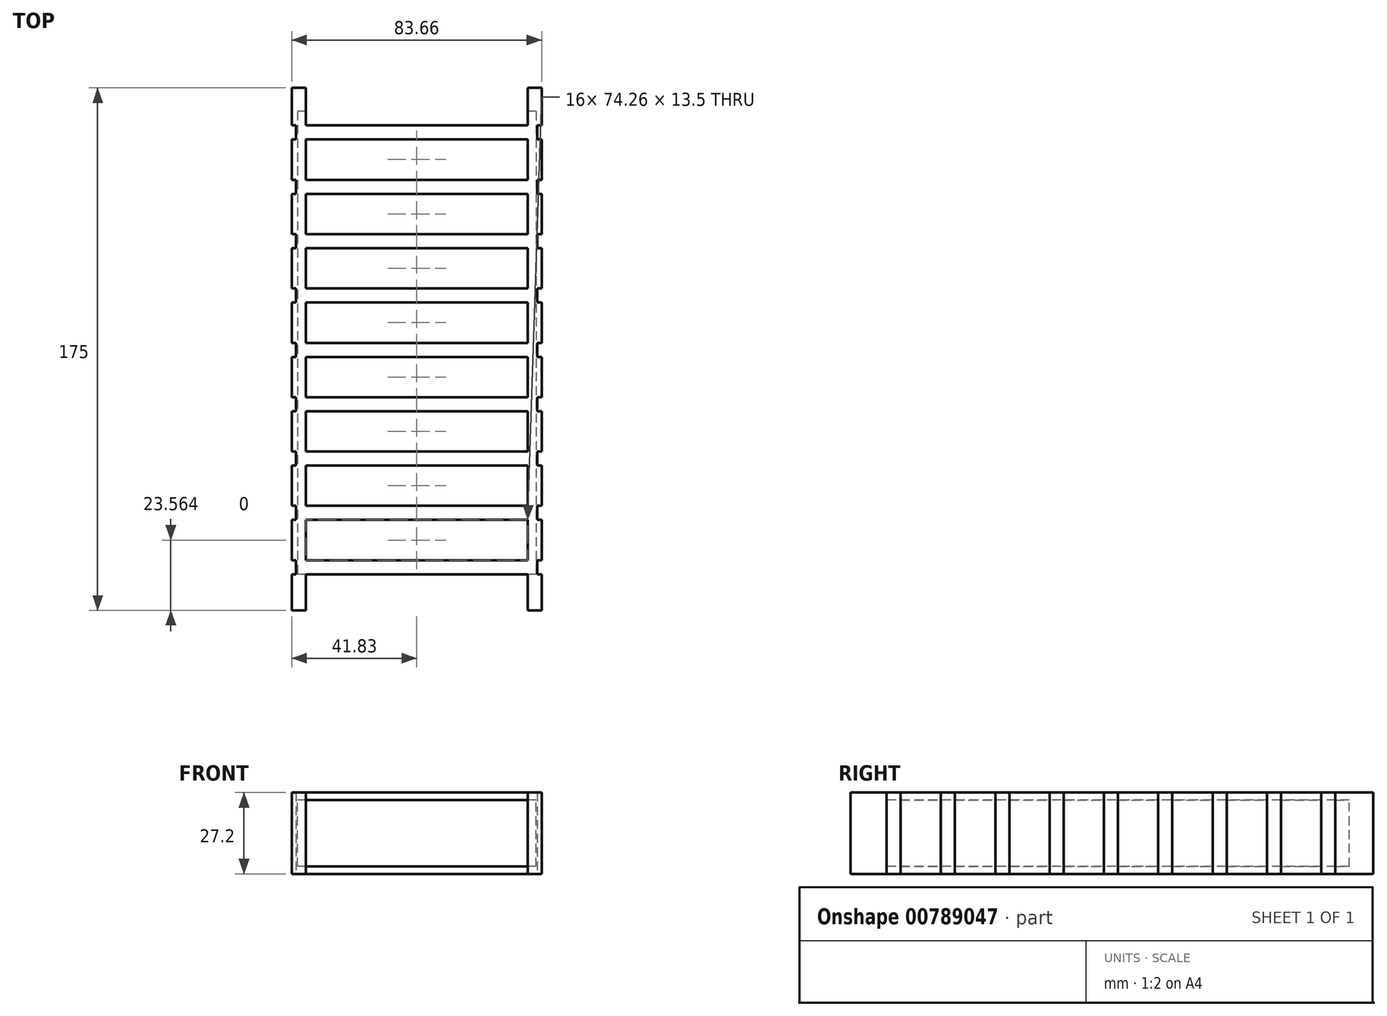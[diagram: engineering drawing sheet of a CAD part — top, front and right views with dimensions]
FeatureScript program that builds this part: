
annotation { "Feature Type Name" : "Feature", "Feature Type Description" : "" }
export const myFeature = defineFeature(function(context is Context, id is Id, definition is map)
    precondition{}
    {
        {
            var Q0;
            Q0=qCreatedBy(makeId("Top.planeOp"),FACE);
            var sketch = newSketch(context, id + "F0", { "sketchPlane" : qUnion([Q0])});
            skLineSegment(sketch, "E0.bottom", {"start": v(-37.13, -87.5) * mm, "end": v(-41.83, -87.5) * mm});
            skLineSegment(sketch, "E0.top", {"start": v(-37.13, 87.5) * mm, "end": v(-41.83, 87.5) * mm});
            skLineSegment(sketch, "E0.left", {"start": v(-37.13, -87.5) * mm, "end": v(-37.13, 87.5) * mm});
            skLineSegment(sketch, "E0.right", {"start": v(-41.83, -87.5) * mm, "end": v(-41.83, 87.5) * mm});
            skPoint(sketch, "E0.middle", {"position": v(-39.48, 0) * mm});
            skLineSegment(sketch, "E1.MirrorCS", {"start": v(37.13, -87.5) * mm, "end": v(41.83, -87.5) * mm});
            skLineSegment(sketch, "E2.MirrorCS", {"start": v(37.13, 87.5) * mm, "end": v(41.83, 87.5) * mm});
            skLineSegment(sketch, "E3.MirrorCS", {"start": v(41.83, -87.5) * mm, "end": v(41.83, 87.5) * mm});
            skLineSegment(sketch, "E4.MirrorCS", {"start": v(37.13, -87.5) * mm, "end": v(37.13, 87.5) * mm});
            skPoint(sketch, "E5.MirrorP", {"position": v(39.48, 0) * mm});
            skLineSegment(sketch, "E6.bottom", {"start": v(40.4, -83.3) * mm, "end": v(-40.4, -83.3) * mm});
            skLineSegment(sketch, "E6.top", {"start": v(40.4, 83.3) * mm, "end": v(-40.4, 83.3) * mm});
            skLineSegment(sketch, "E6.left", {"start": v(40.4, -83.3) * mm, "end": v(40.4, 83.3) * mm});
            skLineSegment(sketch, "E6.right", {"start": v(-40.4, -83.3) * mm, "end": v(-40.4, 83.3) * mm});
            skPoint(sketch, "E6.middle", {"position": v(0, 0) * mm});
            skLineSegment(sketch, "E7.bottom", {"start": v(-41.83, 74.91) * mm, "end": v(41.83, 74.91) * mm});
            skLineSegment(sketch, "E7.top", {"start": v(-41.83, 70.21) * mm, "end": v(41.83, 70.21) * mm});
            skLineSegment(sketch, "E7.left", {"start": v(-41.83, 74.91) * mm, "end": v(-41.83, 70.21) * mm});
            skLineSegment(sketch, "E7.right", {"start": v(41.83, 74.91) * mm, "end": v(41.83, 70.21) * mm});
            skLineSegment(sketch, "E8", {"start": v(50.16, 70.21) * mm, "end": v(50.16, 56.71) * mm});
            skLineSegment(sketch, "E9", {"start": v(50.16, 63.46) * mm, "end": v(43.87, 63.46) * mm});
            skLineSegment(sketch, "E10.MirrorCS", {"start": v(-41.83, 52.01) * mm, "end": v(41.83, 52.01) * mm});
            skLineSegment(sketch, "E11.MirrorCS", {"start": v(41.83, 52.01) * mm, "end": v(41.83, 56.71) * mm});
            skLineSegment(sketch, "E12.MirrorCS", {"start": v(-41.83, 56.71) * mm, "end": v(41.83, 56.71) * mm});
            skLineSegment(sketch, "E13.MirrorCS", {"start": v(-41.83, 52.01) * mm, "end": v(-41.83, 56.71) * mm});
            skLineSegment(sketch, "E14", {"start": v(-5.8, 54.36) * mm, "end": v(6.31, 54.36) * mm});
            skPoint(sketch, "E14.startSnap0", {"position": v(41.83, 54.36) * mm});
            skLineSegment(sketch, "E15.MirrorCS", {"start": v(50.16, 45.26) * mm, "end": v(43.87, 45.26) * mm});
            skLineSegment(sketch, "E16.MirrorCS", {"start": v(50.16, 38.51) * mm, "end": v(50.16, 52.01) * mm});
            skLineSegment(sketch, "E17.MirrorCS", {"start": v(41.83, 38.51) * mm, "end": v(41.83, 33.81) * mm});
            skLineSegment(sketch, "E18.MirrorCS", {"start": v(-41.83, 38.51) * mm, "end": v(41.83, 38.51) * mm});
            skLineSegment(sketch, "E19.MirrorCS", {"start": v(-5.8, 36.16) * mm, "end": v(6.31, 36.16) * mm});
            skLineSegment(sketch, "E20.MirrorCS", {"start": v(-41.83, 33.81) * mm, "end": v(41.83, 33.81) * mm});
            skLineSegment(sketch, "E21.MirrorCS", {"start": v(-41.83, 38.51) * mm, "end": v(-41.83, 33.81) * mm});
            skPoint(sketch, "E22.MirrorP", {"position": v(41.83, 36.16) * mm});
            skPoint(sketch, "E23.MirrorP", {"position": v(41.83, 17.96) * mm});
            skLineSegment(sketch, "E24.MirrorCS", {"start": v(50.16, 27.06) * mm, "end": v(43.87, 27.06) * mm});
            skLineSegment(sketch, "E25.MirrorCS", {"start": v(50.16, 33.81) * mm, "end": v(50.16, 20.31) * mm});
            skLineSegment(sketch, "E26.MirrorCS", {"start": v(41.83, 15.61) * mm, "end": v(41.83, 20.31) * mm});
            skLineSegment(sketch, "E27.MirrorCS", {"start": v(-41.83, 15.61) * mm, "end": v(41.83, 15.61) * mm});
            skLineSegment(sketch, "E28.MirrorCS", {"start": v(-41.83, 20.31) * mm, "end": v(41.83, 20.31) * mm});
            skLineSegment(sketch, "E29.MirrorCS", {"start": v(-5.8, 17.96) * mm, "end": v(6.31, 17.96) * mm});
            skLineSegment(sketch, "E30.MirrorCS", {"start": v(-41.83, 15.61) * mm, "end": v(-41.83, 20.31) * mm});
            skLineSegment(sketch, "E31.MirrorCS", {"start": v(50.16, 8.86) * mm, "end": v(43.87, 8.86) * mm});
            skLineSegment(sketch, "E32.MirrorCS", {"start": v(50.16, 2.11) * mm, "end": v(50.16, 15.61) * mm});
            skPoint(sketch, "E33.MirrorP", {"position": v(41.83, -0.24) * mm});
            skLineSegment(sketch, "E34.MirrorCS", {"start": v(41.83, 2.11) * mm, "end": v(41.83, -2.59) * mm});
            skLineSegment(sketch, "E35.MirrorCS", {"start": v(-41.83, -2.59) * mm, "end": v(41.83, -2.59) * mm});
            skLineSegment(sketch, "E36.MirrorCS", {"start": v(-41.83, 2.11) * mm, "end": v(41.83, 2.11) * mm});
            skLineSegment(sketch, "E37.MirrorCS", {"start": v(-41.83, 2.11) * mm, "end": v(-41.83, -2.59) * mm});
            skLineSegment(sketch, "E38.MirrorCS", {"start": v(-5.8, -0.24) * mm, "end": v(6.31, -0.24) * mm});
            skLineSegment(sketch, "E39.MirrorCS", {"start": v(50.16, -2.59) * mm, "end": v(50.16, -16.09) * mm});
            skLineSegment(sketch, "E40.MirrorCS", {"start": v(50.16, -9.34) * mm, "end": v(43.87, -9.34) * mm});
            skLineSegment(sketch, "E41.MirrorCS", {"start": v(41.83, -20.79) * mm, "end": v(41.83, -16.09) * mm});
            skPoint(sketch, "E42.MirrorP", {"position": v(41.83, -18.44) * mm});
            skLineSegment(sketch, "E43.MirrorCS", {"start": v(-41.83, -20.79) * mm, "end": v(-41.83, -16.09) * mm});
            skPoint(sketch, "E44.MirrorP", {"position": v(39.48, -18.67) * mm});
            skLineSegment(sketch, "E45.MirrorCS", {"start": v(-5.8, -18.44) * mm, "end": v(6.31, -18.44) * mm});
            skLineSegment(sketch, "E46.MirrorCS", {"start": v(-41.83, -20.79) * mm, "end": v(41.83, -20.79) * mm});
            skLineSegment(sketch, "E47.MirrorCS", {"start": v(-41.83, -16.09) * mm, "end": v(41.83, -16.09) * mm});
            skPoint(sketch, "E48.MirrorP", {"position": v(0, -18.67) * mm});
            skPoint(sketch, "E49.MirrorP", {"position": v(-39.48, -18.67) * mm});
            skLineSegment(sketch, "E50.MirrorCS", {"start": v(50.16, -27.54) * mm, "end": v(43.87, -27.54) * mm});
            skLineSegment(sketch, "E51.MirrorCS", {"start": v(50.16, -34.29) * mm, "end": v(50.16, -20.79) * mm});
            skPoint(sketch, "E52.MirrorP", {"position": v(41.83, -36.64) * mm});
            skLineSegment(sketch, "E53.MirrorCS", {"start": v(41.83, -34.29) * mm, "end": v(41.83, -38.99) * mm});
            skPoint(sketch, "E54.MirrorP", {"position": v(0, -36.4) * mm});
            skLineSegment(sketch, "E55.MirrorCS", {"start": v(-41.83, -38.99) * mm, "end": v(41.83, -38.99) * mm});
            skPoint(sketch, "E56.MirrorP", {"position": v(-39.48, -36.4) * mm});
            skPoint(sketch, "E57.MirrorP", {"position": v(39.48, -36.4) * mm});
            skLineSegment(sketch, "E58.MirrorCS", {"start": v(-41.83, -34.29) * mm, "end": v(41.83, -34.29) * mm});
            skLineSegment(sketch, "E59.MirrorCS", {"start": v(-41.83, -34.29) * mm, "end": v(-41.83, -38.99) * mm});
            skLineSegment(sketch, "E60.MirrorCS", {"start": v(-5.8, -36.64) * mm, "end": v(6.31, -36.64) * mm});
            skLineSegment(sketch, "E61.MirrorCS", {"start": v(50.16, -38.99) * mm, "end": v(50.16, -52.49) * mm});
            skLineSegment(sketch, "E62.MirrorCS", {"start": v(50.16, -45.74) * mm, "end": v(43.87, -45.74) * mm});
            skPoint(sketch, "E63.MirrorP", {"position": v(41.83, -54.84) * mm});
            skLineSegment(sketch, "E64.MirrorCS", {"start": v(41.83, -57.19) * mm, "end": v(41.83, -52.49) * mm});
            skPoint(sketch, "E65.MirrorP", {"position": v(-39.48, -55.07) * mm});
            skLineSegment(sketch, "E66.MirrorCS", {"start": v(-5.8, -54.84) * mm, "end": v(6.31, -54.84) * mm});
            skPoint(sketch, "E67.MirrorP", {"position": v(39.48, -55.07) * mm});
            skLineSegment(sketch, "E68.MirrorCS", {"start": v(-41.83, -57.19) * mm, "end": v(41.83, -57.19) * mm});
            skPoint(sketch, "E69.MirrorP", {"position": v(0, -55.07) * mm});
            skLineSegment(sketch, "E70.MirrorCS", {"start": v(-41.83, -52.49) * mm, "end": v(41.83, -52.49) * mm});
            skLineSegment(sketch, "E71.MirrorCS", {"start": v(-41.83, -57.19) * mm, "end": v(-41.83, -52.49) * mm});
            skLineSegment(sketch, "E72.MirrorCS", {"start": v(50.16, -63.94) * mm, "end": v(43.87, -63.94) * mm});
            skLineSegment(sketch, "E73.MirrorCS", {"start": v(50.16, -70.69) * mm, "end": v(50.16, -57.19) * mm});
            skPoint(sketch, "E74.MirrorP", {"position": v(41.83, -73.04) * mm});
            skLineSegment(sketch, "E75.MirrorCS", {"start": v(41.83, -70.69) * mm, "end": v(41.83, -75.39) * mm});
            skLineSegment(sketch, "E76.MirrorCS", {"start": v(-5.8, -73.04) * mm, "end": v(6.31, -73.04) * mm});
            skLineSegment(sketch, "E77.MirrorCS", {"start": v(-41.83, -70.69) * mm, "end": v(41.83, -70.69) * mm});
            skPoint(sketch, "E78.MirrorP", {"position": v(0, -72.8) * mm});
            skPoint(sketch, "E79.MirrorP", {"position": v(-39.48, -72.8) * mm});
            skLineSegment(sketch, "E80.MirrorCS", {"start": v(-41.83, -75.39) * mm, "end": v(41.83, -75.39) * mm});
            skLineSegment(sketch, "E81.MirrorCS", {"start": v(-41.83, -70.69) * mm, "end": v(-41.83, -75.39) * mm});
            skPoint(sketch, "E82.MirrorP", {"position": v(39.48, -72.8) * mm});
            skSolve(sketch);
        }
        {
            var Q0;
            {var subQ1=sQuery(id+"F0.wireOp",EDGE,"E0.top");Q0=makeQuery(id+"F0.imprint","IMPRINT",FACE,{"disambiguationData":[TD([[makeQuery(id+"F0.imprint","IMPRINT",EDGE,{"derivedFrom":subQ1}),1.0]])]});}
            var Q1;
            {var subQ0=sQuery(id+"F0.wireOp",EDGE,"E7.top");var subQ1=sQuery(id+"F0.wireOp",EDGE,"E0.left");var subQ2=makeQuery(id+"F0.imprint","INTERSECT",VERTEX,{"derivedFrom":[subQ1,subQ0]});Q1=makeQuery(id+"F0.imprint","IMPRINT",FACE,{"disambiguationData":[TD([[makeQuery(id+"F0.imprint","IMPRINT",EDGE,{"disambiguationData":[TD([[subQ2,-1.0]])],"derivedFrom":subQ1}),-1.0]])]});}
            var Q2;
            {var subQ0=sQuery(id+"F0.wireOp",EDGE,"E7.top");var subQ1=sQuery(id+"F0.wireOp",EDGE,"E0.left");var subQ2=makeQuery(id+"F0.imprint","INTERSECT",VERTEX,{"derivedFrom":[subQ1,subQ0]});Q2=makeQuery(id+"F0.imprint","IMPRINT",FACE,{"disambiguationData":[TD([[makeQuery(id+"F0.imprint","IMPRINT",EDGE,{"disambiguationData":[TD([[subQ2,-1.0]])],"derivedFrom":subQ1}),1.0]])]});}
            var Q3;
            {var subQ5=sQuery(id+"F0.wireOp",EDGE,"E7.left");Q3=makeQuery(id+"F0.imprint","IMPRINT",FACE,{"disambiguationData":[TD([[makeQuery(id+"F0.imprint","IMPRINT",EDGE,{"derivedFrom":subQ5}),1.0]])]});}
            var Q4;
            {var subQ0=sQuery(id+"F0.wireOp",EDGE,"E6.top");var subQ1=sQuery(id+"F0.wireOp",EDGE,"E4.MirrorCS");var subQ2=makeQuery(id+"F0.imprint","INTERSECT",VERTEX,{"derivedFrom":[subQ1,subQ0]});Q4=makeQuery(id+"F0.imprint","IMPRINT",FACE,{"disambiguationData":[TD([[makeQuery(id+"F0.imprint","IMPRINT",EDGE,{"disambiguationData":[TD([[subQ2,1.0]])],"derivedFrom":subQ1}),-1.0]])]});}
            var Q5;
            {var subQ1=sQuery(id+"F0.wireOp",EDGE,"E2.MirrorCS");Q5=makeQuery(id+"F0.imprint","IMPRINT",FACE,{"disambiguationData":[TD([[makeQuery(id+"F0.imprint","IMPRINT",EDGE,{"derivedFrom":subQ1}),-1.0]])]});}
            var Q6;
            {var subQ0=sQuery(id+"F0.wireOp",EDGE,"E7.top");var subQ1=sQuery(id+"F0.wireOp",EDGE,"E4.MirrorCS");var subQ2=makeQuery(id+"F0.imprint","INTERSECT",VERTEX,{"derivedFrom":[subQ1,subQ0]});Q6=makeQuery(id+"F0.imprint","IMPRINT",FACE,{"disambiguationData":[TD([[makeQuery(id+"F0.imprint","IMPRINT",EDGE,{"disambiguationData":[TD([[subQ2,-1.0]])],"derivedFrom":subQ1}),-1.0]])]});}
            var Q7;
            {var subQ5=sQuery(id+"F0.wireOp",EDGE,"E7.right");Q7=makeQuery(id+"F0.imprint","IMPRINT",FACE,{"disambiguationData":[TD([[makeQuery(id+"F0.imprint","IMPRINT",EDGE,{"derivedFrom":subQ5}),-1.0]])]});}
            var Q8;
            {var subQ3=sQuery(id+"F0.wireOp",EDGE,"E12.MirrorCS");var subQ5=sQuery(id+"F0.wireOp",EDGE,"E6.right");var subQ6=makeQuery(id+"F0.imprint","INTERSECT",VERTEX,{"derivedFrom":[subQ5,subQ3]});Q8=makeQuery(id+"F0.imprint","IMPRINT",FACE,{"disambiguationData":[TD([[makeQuery(id+"F0.imprint","IMPRINT",EDGE,{"disambiguationData":[TD([[subQ6,-1.0]])],"derivedFrom":subQ5}),1.0]])]});}
            var Q9;
            {var subQ0=sQuery(id+"F0.wireOp",EDGE,"E12.MirrorCS");var subQ1=sQuery(id+"F0.wireOp",EDGE,"E0.left");var subQ2=makeQuery(id+"F0.imprint","INTERSECT",VERTEX,{"derivedFrom":[subQ1,subQ0]});Q9=makeQuery(id+"F0.imprint","IMPRINT",FACE,{"disambiguationData":[TD([[makeQuery(id+"F0.imprint","IMPRINT",EDGE,{"disambiguationData":[TD([[subQ2,-1.0]])],"derivedFrom":subQ1}),1.0]])]});}
            var Q10;
            {var subQ0=sQuery(id+"F0.wireOp",EDGE,"E12.MirrorCS");var subQ1=sQuery(id+"F0.wireOp",EDGE,"E4.MirrorCS");var subQ2=makeQuery(id+"F0.imprint","INTERSECT",VERTEX,{"derivedFrom":[subQ1,subQ0]});Q10=makeQuery(id+"F0.imprint","IMPRINT",FACE,{"disambiguationData":[TD([[makeQuery(id+"F0.imprint","IMPRINT",EDGE,{"disambiguationData":[TD([[subQ2,-1.0]])],"derivedFrom":subQ1}),-1.0]])]});}
            var Q11;
            {var subQ3=sQuery(id+"F0.wireOp",EDGE,"E12.MirrorCS");var subQ5=sQuery(id+"F0.wireOp",EDGE,"E6.left");var subQ6=makeQuery(id+"F0.imprint","INTERSECT",VERTEX,{"derivedFrom":[subQ5,subQ3]});Q11=makeQuery(id+"F0.imprint","IMPRINT",FACE,{"disambiguationData":[TD([[makeQuery(id+"F0.imprint","IMPRINT",EDGE,{"disambiguationData":[TD([[subQ6,-1.0]])],"derivedFrom":subQ5}),-1.0]])]});}
            var Q12;
            {var subQ5=sQuery(id+"F0.wireOp",EDGE,"E11.MirrorCS");Q12=makeQuery(id+"F0.imprint","IMPRINT",FACE,{"disambiguationData":[TD([[makeQuery(id+"F0.imprint","IMPRINT",EDGE,{"derivedFrom":subQ5}),1.0]])]});}
            var Q13;
            {var subQ0=sQuery(id+"F0.wireOp",EDGE,"E10.MirrorCS");var subQ1=sQuery(id+"F0.wireOp",EDGE,"E4.MirrorCS");var subQ2=makeQuery(id+"F0.imprint","INTERSECT",VERTEX,{"derivedFrom":[subQ1,subQ0]});Q13=makeQuery(id+"F0.imprint","IMPRINT",FACE,{"disambiguationData":[TD([[makeQuery(id+"F0.imprint","IMPRINT",EDGE,{"disambiguationData":[TD([[subQ2,-1.0]])],"derivedFrom":subQ1}),-1.0]])]});}
            var Q14;
            {var subQ0=sQuery(id+"F0.wireOp",EDGE,"E10.MirrorCS");var subQ1=sQuery(id+"F0.wireOp",EDGE,"E0.left");var subQ2=makeQuery(id+"F0.imprint","INTERSECT",VERTEX,{"derivedFrom":[subQ1,subQ0]});Q14=makeQuery(id+"F0.imprint","IMPRINT",FACE,{"disambiguationData":[TD([[makeQuery(id+"F0.imprint","IMPRINT",EDGE,{"disambiguationData":[TD([[subQ2,-1.0]])],"derivedFrom":subQ1}),-1.0]])]});}
            var Q15;
            {var subQ5=sQuery(id+"F0.wireOp",EDGE,"E13.MirrorCS");Q15=makeQuery(id+"F0.imprint","IMPRINT",FACE,{"disambiguationData":[TD([[makeQuery(id+"F0.imprint","IMPRINT",EDGE,{"derivedFrom":subQ5}),-1.0]])]});}
            var Q16;
            {var subQ0=sQuery(id+"F0.wireOp",EDGE,"E10.MirrorCS");var subQ1=sQuery(id+"F0.wireOp",EDGE,"E0.left");var subQ2=makeQuery(id+"F0.imprint","INTERSECT",VERTEX,{"derivedFrom":[subQ1,subQ0]});Q16=makeQuery(id+"F0.imprint","IMPRINT",FACE,{"disambiguationData":[TD([[makeQuery(id+"F0.imprint","IMPRINT",EDGE,{"disambiguationData":[TD([[subQ2,-1.0]])],"derivedFrom":subQ1}),1.0]])]});}
            var Q17;
            {var subQ3=sQuery(id+"F0.wireOp",EDGE,"E18.MirrorCS");var subQ5=sQuery(id+"F0.wireOp",EDGE,"E6.right");var subQ6=makeQuery(id+"F0.imprint","INTERSECT",VERTEX,{"derivedFrom":[subQ5,subQ3]});Q17=makeQuery(id+"F0.imprint","IMPRINT",FACE,{"disambiguationData":[TD([[makeQuery(id+"F0.imprint","IMPRINT",EDGE,{"disambiguationData":[TD([[subQ6,-1.0]])],"derivedFrom":subQ5}),1.0]])]});}
            var Q18;
            {var subQ0=sQuery(id+"F0.wireOp",EDGE,"E18.MirrorCS");var subQ1=sQuery(id+"F0.wireOp",EDGE,"E0.left");var subQ2=makeQuery(id+"F0.imprint","INTERSECT",VERTEX,{"derivedFrom":[subQ1,subQ0]});Q18=makeQuery(id+"F0.imprint","IMPRINT",FACE,{"disambiguationData":[TD([[makeQuery(id+"F0.imprint","IMPRINT",EDGE,{"disambiguationData":[TD([[subQ2,-1.0]])],"derivedFrom":subQ1}),1.0]])]});}
            var Q19;
            {var subQ0=sQuery(id+"F0.wireOp",EDGE,"E18.MirrorCS");var subQ1=sQuery(id+"F0.wireOp",EDGE,"E4.MirrorCS");var subQ2=makeQuery(id+"F0.imprint","INTERSECT",VERTEX,{"derivedFrom":[subQ1,subQ0]});Q19=makeQuery(id+"F0.imprint","IMPRINT",FACE,{"disambiguationData":[TD([[makeQuery(id+"F0.imprint","IMPRINT",EDGE,{"disambiguationData":[TD([[subQ2,-1.0]])],"derivedFrom":subQ1}),-1.0]])]});}
            var Q20;
            {var subQ3=sQuery(id+"F0.wireOp",EDGE,"E18.MirrorCS");var subQ5=sQuery(id+"F0.wireOp",EDGE,"E6.left");var subQ6=makeQuery(id+"F0.imprint","INTERSECT",VERTEX,{"derivedFrom":[subQ5,subQ3]});Q20=makeQuery(id+"F0.imprint","IMPRINT",FACE,{"disambiguationData":[TD([[makeQuery(id+"F0.imprint","IMPRINT",EDGE,{"disambiguationData":[TD([[subQ6,-1.0]])],"derivedFrom":subQ5}),-1.0]])]});}
            var Q21;
            {var subQ5=sQuery(id+"F0.wireOp",EDGE,"E21.MirrorCS");Q21=makeQuery(id+"F0.imprint","IMPRINT",FACE,{"disambiguationData":[TD([[makeQuery(id+"F0.imprint","IMPRINT",EDGE,{"derivedFrom":subQ5}),1.0]])]});}
            var Q22;
            {var subQ0=sQuery(id+"F0.wireOp",EDGE,"E20.MirrorCS");var subQ1=sQuery(id+"F0.wireOp",EDGE,"E0.left");var subQ2=makeQuery(id+"F0.imprint","INTERSECT",VERTEX,{"derivedFrom":[subQ1,subQ0]});Q22=makeQuery(id+"F0.imprint","IMPRINT",FACE,{"disambiguationData":[TD([[makeQuery(id+"F0.imprint","IMPRINT",EDGE,{"disambiguationData":[TD([[subQ2,-1.0]])],"derivedFrom":subQ1}),1.0]])]});}
            var Q23;
            {var subQ0=sQuery(id+"F0.wireOp",EDGE,"E20.MirrorCS");var subQ1=sQuery(id+"F0.wireOp",EDGE,"E0.left");var subQ2=makeQuery(id+"F0.imprint","INTERSECT",VERTEX,{"derivedFrom":[subQ1,subQ0]});Q23=makeQuery(id+"F0.imprint","IMPRINT",FACE,{"disambiguationData":[TD([[makeQuery(id+"F0.imprint","IMPRINT",EDGE,{"disambiguationData":[TD([[subQ2,-1.0]])],"derivedFrom":subQ1}),-1.0]])]});}
            var Q24;
            {var subQ0=sQuery(id+"F0.wireOp",EDGE,"E20.MirrorCS");var subQ1=sQuery(id+"F0.wireOp",EDGE,"E4.MirrorCS");var subQ2=makeQuery(id+"F0.imprint","INTERSECT",VERTEX,{"derivedFrom":[subQ1,subQ0]});Q24=makeQuery(id+"F0.imprint","IMPRINT",FACE,{"disambiguationData":[TD([[makeQuery(id+"F0.imprint","IMPRINT",EDGE,{"disambiguationData":[TD([[subQ2,-1.0]])],"derivedFrom":subQ1}),-1.0]])]});}
            var Q25;
            {var subQ5=sQuery(id+"F0.wireOp",EDGE,"E17.MirrorCS");Q25=makeQuery(id+"F0.imprint","IMPRINT",FACE,{"disambiguationData":[TD([[makeQuery(id+"F0.imprint","IMPRINT",EDGE,{"derivedFrom":subQ5}),-1.0]])]});}
            var Q26;
            {var subQ3=sQuery(id+"F0.wireOp",EDGE,"E28.MirrorCS");var subQ5=sQuery(id+"F0.wireOp",EDGE,"E6.right");var subQ6=makeQuery(id+"F0.imprint","INTERSECT",VERTEX,{"derivedFrom":[subQ5,subQ3]});Q26=makeQuery(id+"F0.imprint","IMPRINT",FACE,{"disambiguationData":[TD([[makeQuery(id+"F0.imprint","IMPRINT",EDGE,{"disambiguationData":[TD([[subQ6,-1.0]])],"derivedFrom":subQ5}),1.0]])]});}
            var Q27;
            {var subQ0=sQuery(id+"F0.wireOp",EDGE,"E28.MirrorCS");var subQ1=sQuery(id+"F0.wireOp",EDGE,"E0.left");var subQ2=makeQuery(id+"F0.imprint","INTERSECT",VERTEX,{"derivedFrom":[subQ1,subQ0]});Q27=makeQuery(id+"F0.imprint","IMPRINT",FACE,{"disambiguationData":[TD([[makeQuery(id+"F0.imprint","IMPRINT",EDGE,{"disambiguationData":[TD([[subQ2,-1.0]])],"derivedFrom":subQ1}),1.0]])]});}
            var Q28;
            {var subQ0=sQuery(id+"F0.wireOp",EDGE,"E28.MirrorCS");var subQ1=sQuery(id+"F0.wireOp",EDGE,"E4.MirrorCS");var subQ2=makeQuery(id+"F0.imprint","INTERSECT",VERTEX,{"derivedFrom":[subQ1,subQ0]});Q28=makeQuery(id+"F0.imprint","IMPRINT",FACE,{"disambiguationData":[TD([[makeQuery(id+"F0.imprint","IMPRINT",EDGE,{"disambiguationData":[TD([[subQ2,-1.0]])],"derivedFrom":subQ1}),-1.0]])]});}
            var Q29;
            {var subQ3=sQuery(id+"F0.wireOp",EDGE,"E28.MirrorCS");var subQ5=sQuery(id+"F0.wireOp",EDGE,"E6.left");var subQ6=makeQuery(id+"F0.imprint","INTERSECT",VERTEX,{"derivedFrom":[subQ5,subQ3]});Q29=makeQuery(id+"F0.imprint","IMPRINT",FACE,{"disambiguationData":[TD([[makeQuery(id+"F0.imprint","IMPRINT",EDGE,{"disambiguationData":[TD([[subQ6,-1.0]])],"derivedFrom":subQ5}),-1.0]])]});}
            var Q30;
            {var subQ5=sQuery(id+"F0.wireOp",EDGE,"E30.MirrorCS");Q30=makeQuery(id+"F0.imprint","IMPRINT",FACE,{"disambiguationData":[TD([[makeQuery(id+"F0.imprint","IMPRINT",EDGE,{"derivedFrom":subQ5}),-1.0]])]});}
            var Q31;
            {var subQ0=sQuery(id+"F0.wireOp",EDGE,"E27.MirrorCS");var subQ1=sQuery(id+"F0.wireOp",EDGE,"E0.left");var subQ2=makeQuery(id+"F0.imprint","INTERSECT",VERTEX,{"derivedFrom":[subQ1,subQ0]});Q31=makeQuery(id+"F0.imprint","IMPRINT",FACE,{"disambiguationData":[TD([[makeQuery(id+"F0.imprint","IMPRINT",EDGE,{"disambiguationData":[TD([[subQ2,-1.0]])],"derivedFrom":subQ1}),1.0]])]});}
            var Q32;
            {var subQ0=sQuery(id+"F0.wireOp",EDGE,"E27.MirrorCS");var subQ1=sQuery(id+"F0.wireOp",EDGE,"E0.left");var subQ2=makeQuery(id+"F0.imprint","INTERSECT",VERTEX,{"derivedFrom":[subQ1,subQ0]});Q32=makeQuery(id+"F0.imprint","IMPRINT",FACE,{"disambiguationData":[TD([[makeQuery(id+"F0.imprint","IMPRINT",EDGE,{"disambiguationData":[TD([[subQ2,-1.0]])],"derivedFrom":subQ1}),-1.0]])]});}
            var Q33;
            {var subQ0=sQuery(id+"F0.wireOp",EDGE,"E27.MirrorCS");var subQ1=sQuery(id+"F0.wireOp",EDGE,"E4.MirrorCS");var subQ2=makeQuery(id+"F0.imprint","INTERSECT",VERTEX,{"derivedFrom":[subQ1,subQ0]});Q33=makeQuery(id+"F0.imprint","IMPRINT",FACE,{"disambiguationData":[TD([[makeQuery(id+"F0.imprint","IMPRINT",EDGE,{"disambiguationData":[TD([[subQ2,-1.0]])],"derivedFrom":subQ1}),-1.0]])]});}
            var Q34;
            {var subQ5=sQuery(id+"F0.wireOp",EDGE,"E26.MirrorCS");Q34=makeQuery(id+"F0.imprint","IMPRINT",FACE,{"disambiguationData":[TD([[makeQuery(id+"F0.imprint","IMPRINT",EDGE,{"derivedFrom":subQ5}),1.0]])]});}
            var Q35;
            {var subQ3=sQuery(id+"F0.wireOp",EDGE,"E36.MirrorCS");var subQ5=sQuery(id+"F0.wireOp",EDGE,"E6.right");var subQ6=makeQuery(id+"F0.imprint","INTERSECT",VERTEX,{"derivedFrom":[subQ5,subQ3]});Q35=makeQuery(id+"F0.imprint","IMPRINT",FACE,{"disambiguationData":[TD([[makeQuery(id+"F0.imprint","IMPRINT",EDGE,{"disambiguationData":[TD([[subQ6,-1.0]])],"derivedFrom":subQ5}),1.0]])]});}
            var Q36;
            {var subQ0=sQuery(id+"F0.wireOp",EDGE,"E36.MirrorCS");var subQ1=sQuery(id+"F0.wireOp",EDGE,"E0.left");var subQ2=makeQuery(id+"F0.imprint","INTERSECT",VERTEX,{"derivedFrom":[subQ1,subQ0]});Q36=makeQuery(id+"F0.imprint","IMPRINT",FACE,{"disambiguationData":[TD([[makeQuery(id+"F0.imprint","IMPRINT",EDGE,{"disambiguationData":[TD([[subQ2,-1.0]])],"derivedFrom":subQ1}),1.0]])]});}
            var Q37;
            {var subQ5=sQuery(id+"F0.wireOp",EDGE,"E37.MirrorCS");Q37=makeQuery(id+"F0.imprint","IMPRINT",FACE,{"disambiguationData":[TD([[makeQuery(id+"F0.imprint","IMPRINT",EDGE,{"derivedFrom":subQ5}),1.0]])]});}
            var Q38;
            {var subQ0=sQuery(id+"F0.wireOp",EDGE,"E35.MirrorCS");var subQ1=sQuery(id+"F0.wireOp",EDGE,"E0.left");var subQ2=makeQuery(id+"F0.imprint","INTERSECT",VERTEX,{"derivedFrom":[subQ1,subQ0]});Q38=makeQuery(id+"F0.imprint","IMPRINT",FACE,{"disambiguationData":[TD([[makeQuery(id+"F0.imprint","IMPRINT",EDGE,{"disambiguationData":[TD([[subQ2,-1.0]])],"derivedFrom":subQ1}),1.0]])]});}
            var Q39;
            {var subQ0=sQuery(id+"F0.wireOp",EDGE,"E35.MirrorCS");var subQ1=sQuery(id+"F0.wireOp",EDGE,"E0.left");var subQ2=makeQuery(id+"F0.imprint","INTERSECT",VERTEX,{"derivedFrom":[subQ1,subQ0]});Q39=makeQuery(id+"F0.imprint","IMPRINT",FACE,{"disambiguationData":[TD([[makeQuery(id+"F0.imprint","IMPRINT",EDGE,{"disambiguationData":[TD([[subQ2,-1.0]])],"derivedFrom":subQ1}),-1.0]])]});}
            var Q40;
            {var subQ0=sQuery(id+"F0.wireOp",EDGE,"E36.MirrorCS");var subQ1=sQuery(id+"F0.wireOp",EDGE,"E4.MirrorCS");var subQ2=makeQuery(id+"F0.imprint","INTERSECT",VERTEX,{"derivedFrom":[subQ1,subQ0]});Q40=makeQuery(id+"F0.imprint","IMPRINT",FACE,{"disambiguationData":[TD([[makeQuery(id+"F0.imprint","IMPRINT",EDGE,{"disambiguationData":[TD([[subQ2,-1.0]])],"derivedFrom":subQ1}),-1.0]])]});}
            var Q41;
            {var subQ3=sQuery(id+"F0.wireOp",EDGE,"E36.MirrorCS");var subQ5=sQuery(id+"F0.wireOp",EDGE,"E6.left");var subQ6=makeQuery(id+"F0.imprint","INTERSECT",VERTEX,{"derivedFrom":[subQ5,subQ3]});Q41=makeQuery(id+"F0.imprint","IMPRINT",FACE,{"disambiguationData":[TD([[makeQuery(id+"F0.imprint","IMPRINT",EDGE,{"disambiguationData":[TD([[subQ6,-1.0]])],"derivedFrom":subQ5}),-1.0]])]});}
            var Q42;
            {var subQ0=sQuery(id+"F0.wireOp",EDGE,"E35.MirrorCS");var subQ1=sQuery(id+"F0.wireOp",EDGE,"E4.MirrorCS");var subQ2=makeQuery(id+"F0.imprint","INTERSECT",VERTEX,{"derivedFrom":[subQ1,subQ0]});Q42=makeQuery(id+"F0.imprint","IMPRINT",FACE,{"disambiguationData":[TD([[makeQuery(id+"F0.imprint","IMPRINT",EDGE,{"disambiguationData":[TD([[subQ2,-1.0]])],"derivedFrom":subQ1}),-1.0]])]});}
            var Q43;
            {var subQ5=sQuery(id+"F0.wireOp",EDGE,"E34.MirrorCS");Q43=makeQuery(id+"F0.imprint","IMPRINT",FACE,{"disambiguationData":[TD([[makeQuery(id+"F0.imprint","IMPRINT",EDGE,{"derivedFrom":subQ5}),-1.0]])]});}
            var Q44;
            {var subQ3=sQuery(id+"F0.wireOp",EDGE,"E47.MirrorCS");var subQ5=sQuery(id+"F0.wireOp",EDGE,"E6.right");var subQ6=makeQuery(id+"F0.imprint","INTERSECT",VERTEX,{"derivedFrom":[subQ5,subQ3]});Q44=makeQuery(id+"F0.imprint","IMPRINT",FACE,{"disambiguationData":[TD([[makeQuery(id+"F0.imprint","IMPRINT",EDGE,{"disambiguationData":[TD([[subQ6,-1.0]])],"derivedFrom":subQ5}),1.0]])]});}
            var Q45;
            {var subQ0=sQuery(id+"F0.wireOp",EDGE,"E47.MirrorCS");var subQ1=sQuery(id+"F0.wireOp",EDGE,"E0.left");var subQ2=makeQuery(id+"F0.imprint","INTERSECT",VERTEX,{"derivedFrom":[subQ1,subQ0]});Q45=makeQuery(id+"F0.imprint","IMPRINT",FACE,{"disambiguationData":[TD([[makeQuery(id+"F0.imprint","IMPRINT",EDGE,{"disambiguationData":[TD([[subQ2,-1.0]])],"derivedFrom":subQ1}),1.0]])]});}
            var Q46;
            {var subQ5=sQuery(id+"F0.wireOp",EDGE,"E43.MirrorCS");Q46=makeQuery(id+"F0.imprint","IMPRINT",FACE,{"disambiguationData":[TD([[makeQuery(id+"F0.imprint","IMPRINT",EDGE,{"derivedFrom":subQ5}),-1.0]])]});}
            var Q47;
            {var subQ0=sQuery(id+"F0.wireOp",EDGE,"E46.MirrorCS");var subQ1=sQuery(id+"F0.wireOp",EDGE,"E0.left");var subQ2=makeQuery(id+"F0.imprint","INTERSECT",VERTEX,{"derivedFrom":[subQ1,subQ0]});Q47=makeQuery(id+"F0.imprint","IMPRINT",FACE,{"disambiguationData":[TD([[makeQuery(id+"F0.imprint","IMPRINT",EDGE,{"disambiguationData":[TD([[subQ2,-1.0]])],"derivedFrom":subQ1}),1.0]])]});}
            var Q48;
            {var subQ0=sQuery(id+"F0.wireOp",EDGE,"E46.MirrorCS");var subQ1=sQuery(id+"F0.wireOp",EDGE,"E0.left");var subQ2=makeQuery(id+"F0.imprint","INTERSECT",VERTEX,{"derivedFrom":[subQ1,subQ0]});Q48=makeQuery(id+"F0.imprint","IMPRINT",FACE,{"disambiguationData":[TD([[makeQuery(id+"F0.imprint","IMPRINT",EDGE,{"disambiguationData":[TD([[subQ2,-1.0]])],"derivedFrom":subQ1}),-1.0]])]});}
            var Q49;
            {var subQ0=sQuery(id+"F0.wireOp",EDGE,"E47.MirrorCS");var subQ1=sQuery(id+"F0.wireOp",EDGE,"E4.MirrorCS");var subQ2=makeQuery(id+"F0.imprint","INTERSECT",VERTEX,{"derivedFrom":[subQ1,subQ0]});Q49=makeQuery(id+"F0.imprint","IMPRINT",FACE,{"disambiguationData":[TD([[makeQuery(id+"F0.imprint","IMPRINT",EDGE,{"disambiguationData":[TD([[subQ2,-1.0]])],"derivedFrom":subQ1}),-1.0]])]});}
            var Q50;
            {var subQ3=sQuery(id+"F0.wireOp",EDGE,"E47.MirrorCS");var subQ5=sQuery(id+"F0.wireOp",EDGE,"E6.left");var subQ6=makeQuery(id+"F0.imprint","INTERSECT",VERTEX,{"derivedFrom":[subQ5,subQ3]});Q50=makeQuery(id+"F0.imprint","IMPRINT",FACE,{"disambiguationData":[TD([[makeQuery(id+"F0.imprint","IMPRINT",EDGE,{"disambiguationData":[TD([[subQ6,-1.0]])],"derivedFrom":subQ5}),-1.0]])]});}
            var Q51;
            {var subQ0=sQuery(id+"F0.wireOp",EDGE,"E46.MirrorCS");var subQ1=sQuery(id+"F0.wireOp",EDGE,"E4.MirrorCS");var subQ2=makeQuery(id+"F0.imprint","INTERSECT",VERTEX,{"derivedFrom":[subQ1,subQ0]});Q51=makeQuery(id+"F0.imprint","IMPRINT",FACE,{"disambiguationData":[TD([[makeQuery(id+"F0.imprint","IMPRINT",EDGE,{"disambiguationData":[TD([[subQ2,-1.0]])],"derivedFrom":subQ1}),-1.0]])]});}
            var Q52;
            {var subQ5=sQuery(id+"F0.wireOp",EDGE,"E41.MirrorCS");Q52=makeQuery(id+"F0.imprint","IMPRINT",FACE,{"disambiguationData":[TD([[makeQuery(id+"F0.imprint","IMPRINT",EDGE,{"derivedFrom":subQ5}),1.0]])]});}
            var Q53;
            {var subQ3=sQuery(id+"F0.wireOp",EDGE,"E58.MirrorCS");var subQ5=sQuery(id+"F0.wireOp",EDGE,"E6.right");var subQ6=makeQuery(id+"F0.imprint","INTERSECT",VERTEX,{"derivedFrom":[subQ5,subQ3]});Q53=makeQuery(id+"F0.imprint","IMPRINT",FACE,{"disambiguationData":[TD([[makeQuery(id+"F0.imprint","IMPRINT",EDGE,{"disambiguationData":[TD([[subQ6,-1.0]])],"derivedFrom":subQ5}),1.0]])]});}
            var Q54;
            {var subQ0=sQuery(id+"F0.wireOp",EDGE,"E58.MirrorCS");var subQ1=sQuery(id+"F0.wireOp",EDGE,"E0.left");var subQ2=makeQuery(id+"F0.imprint","INTERSECT",VERTEX,{"derivedFrom":[subQ1,subQ0]});Q54=makeQuery(id+"F0.imprint","IMPRINT",FACE,{"disambiguationData":[TD([[makeQuery(id+"F0.imprint","IMPRINT",EDGE,{"disambiguationData":[TD([[subQ2,-1.0]])],"derivedFrom":subQ1}),1.0]])]});}
            var Q55;
            {var subQ0=sQuery(id+"F0.wireOp",EDGE,"E58.MirrorCS");var subQ1=sQuery(id+"F0.wireOp",EDGE,"E4.MirrorCS");var subQ2=makeQuery(id+"F0.imprint","INTERSECT",VERTEX,{"derivedFrom":[subQ1,subQ0]});Q55=makeQuery(id+"F0.imprint","IMPRINT",FACE,{"disambiguationData":[TD([[makeQuery(id+"F0.imprint","IMPRINT",EDGE,{"disambiguationData":[TD([[subQ2,-1.0]])],"derivedFrom":subQ1}),-1.0]])]});}
            var Q56;
            {var subQ3=sQuery(id+"F0.wireOp",EDGE,"E58.MirrorCS");var subQ5=sQuery(id+"F0.wireOp",EDGE,"E6.left");var subQ6=makeQuery(id+"F0.imprint","INTERSECT",VERTEX,{"derivedFrom":[subQ5,subQ3]});Q56=makeQuery(id+"F0.imprint","IMPRINT",FACE,{"disambiguationData":[TD([[makeQuery(id+"F0.imprint","IMPRINT",EDGE,{"disambiguationData":[TD([[subQ6,-1.0]])],"derivedFrom":subQ5}),-1.0]])]});}
            var Q57;
            {var subQ5=sQuery(id+"F0.wireOp",EDGE,"E59.MirrorCS");Q57=makeQuery(id+"F0.imprint","IMPRINT",FACE,{"disambiguationData":[TD([[makeQuery(id+"F0.imprint","IMPRINT",EDGE,{"derivedFrom":subQ5}),1.0]])]});}
            var Q58;
            {var subQ0=sQuery(id+"F0.wireOp",EDGE,"E55.MirrorCS");var subQ1=sQuery(id+"F0.wireOp",EDGE,"E0.left");var subQ2=makeQuery(id+"F0.imprint","INTERSECT",VERTEX,{"derivedFrom":[subQ1,subQ0]});Q58=makeQuery(id+"F0.imprint","IMPRINT",FACE,{"disambiguationData":[TD([[makeQuery(id+"F0.imprint","IMPRINT",EDGE,{"disambiguationData":[TD([[subQ2,-1.0]])],"derivedFrom":subQ1}),1.0]])]});}
            var Q59;
            {var subQ0=sQuery(id+"F0.wireOp",EDGE,"E55.MirrorCS");var subQ1=sQuery(id+"F0.wireOp",EDGE,"E0.left");var subQ2=makeQuery(id+"F0.imprint","INTERSECT",VERTEX,{"derivedFrom":[subQ1,subQ0]});Q59=makeQuery(id+"F0.imprint","IMPRINT",FACE,{"disambiguationData":[TD([[makeQuery(id+"F0.imprint","IMPRINT",EDGE,{"disambiguationData":[TD([[subQ2,-1.0]])],"derivedFrom":subQ1}),-1.0]])]});}
            var Q60;
            {var subQ0=sQuery(id+"F0.wireOp",EDGE,"E55.MirrorCS");var subQ1=sQuery(id+"F0.wireOp",EDGE,"E4.MirrorCS");var subQ2=makeQuery(id+"F0.imprint","INTERSECT",VERTEX,{"derivedFrom":[subQ1,subQ0]});Q60=makeQuery(id+"F0.imprint","IMPRINT",FACE,{"disambiguationData":[TD([[makeQuery(id+"F0.imprint","IMPRINT",EDGE,{"disambiguationData":[TD([[subQ2,-1.0]])],"derivedFrom":subQ1}),-1.0]])]});}
            var Q61;
            {var subQ5=sQuery(id+"F0.wireOp",EDGE,"E53.MirrorCS");Q61=makeQuery(id+"F0.imprint","IMPRINT",FACE,{"disambiguationData":[TD([[makeQuery(id+"F0.imprint","IMPRINT",EDGE,{"derivedFrom":subQ5}),-1.0]])]});}
            var Q62;
            {var subQ3=sQuery(id+"F0.wireOp",EDGE,"E70.MirrorCS");var subQ5=sQuery(id+"F0.wireOp",EDGE,"E6.right");var subQ6=makeQuery(id+"F0.imprint","INTERSECT",VERTEX,{"derivedFrom":[subQ5,subQ3]});Q62=makeQuery(id+"F0.imprint","IMPRINT",FACE,{"disambiguationData":[TD([[makeQuery(id+"F0.imprint","IMPRINT",EDGE,{"disambiguationData":[TD([[subQ6,-1.0]])],"derivedFrom":subQ5}),1.0]])]});}
            var Q63;
            {var subQ0=sQuery(id+"F0.wireOp",EDGE,"E70.MirrorCS");var subQ1=sQuery(id+"F0.wireOp",EDGE,"E0.left");var subQ2=makeQuery(id+"F0.imprint","INTERSECT",VERTEX,{"derivedFrom":[subQ1,subQ0]});Q63=makeQuery(id+"F0.imprint","IMPRINT",FACE,{"disambiguationData":[TD([[makeQuery(id+"F0.imprint","IMPRINT",EDGE,{"disambiguationData":[TD([[subQ2,-1.0]])],"derivedFrom":subQ1}),1.0]])]});}
            var Q64;
            {var subQ5=sQuery(id+"F0.wireOp",EDGE,"E71.MirrorCS");Q64=makeQuery(id+"F0.imprint","IMPRINT",FACE,{"disambiguationData":[TD([[makeQuery(id+"F0.imprint","IMPRINT",EDGE,{"derivedFrom":subQ5}),-1.0]])]});}
            var Q65;
            {var subQ0=sQuery(id+"F0.wireOp",EDGE,"E68.MirrorCS");var subQ1=sQuery(id+"F0.wireOp",EDGE,"E0.left");var subQ2=makeQuery(id+"F0.imprint","INTERSECT",VERTEX,{"derivedFrom":[subQ1,subQ0]});Q65=makeQuery(id+"F0.imprint","IMPRINT",FACE,{"disambiguationData":[TD([[makeQuery(id+"F0.imprint","IMPRINT",EDGE,{"disambiguationData":[TD([[subQ2,-1.0]])],"derivedFrom":subQ1}),1.0]])]});}
            var Q66;
            {var subQ0=sQuery(id+"F0.wireOp",EDGE,"E68.MirrorCS");var subQ1=sQuery(id+"F0.wireOp",EDGE,"E0.left");var subQ2=makeQuery(id+"F0.imprint","INTERSECT",VERTEX,{"derivedFrom":[subQ1,subQ0]});Q66=makeQuery(id+"F0.imprint","IMPRINT",FACE,{"disambiguationData":[TD([[makeQuery(id+"F0.imprint","IMPRINT",EDGE,{"disambiguationData":[TD([[subQ2,-1.0]])],"derivedFrom":subQ1}),-1.0]])]});}
            var Q67;
            {var subQ0=sQuery(id+"F0.wireOp",EDGE,"E68.MirrorCS");var subQ1=sQuery(id+"F0.wireOp",EDGE,"E4.MirrorCS");var subQ2=makeQuery(id+"F0.imprint","INTERSECT",VERTEX,{"derivedFrom":[subQ1,subQ0]});Q67=makeQuery(id+"F0.imprint","IMPRINT",FACE,{"disambiguationData":[TD([[makeQuery(id+"F0.imprint","IMPRINT",EDGE,{"disambiguationData":[TD([[subQ2,-1.0]])],"derivedFrom":subQ1}),-1.0]])]});}
            var Q68;
            {var subQ5=sQuery(id+"F0.wireOp",EDGE,"E64.MirrorCS");Q68=makeQuery(id+"F0.imprint","IMPRINT",FACE,{"disambiguationData":[TD([[makeQuery(id+"F0.imprint","IMPRINT",EDGE,{"derivedFrom":subQ5}),1.0]])]});}
            var Q69;
            {var subQ0=sQuery(id+"F0.wireOp",EDGE,"E70.MirrorCS");var subQ1=sQuery(id+"F0.wireOp",EDGE,"E4.MirrorCS");var subQ2=makeQuery(id+"F0.imprint","INTERSECT",VERTEX,{"derivedFrom":[subQ1,subQ0]});Q69=makeQuery(id+"F0.imprint","IMPRINT",FACE,{"disambiguationData":[TD([[makeQuery(id+"F0.imprint","IMPRINT",EDGE,{"disambiguationData":[TD([[subQ2,-1.0]])],"derivedFrom":subQ1}),-1.0]])]});}
            var Q70;
            {var subQ3=sQuery(id+"F0.wireOp",EDGE,"E70.MirrorCS");var subQ5=sQuery(id+"F0.wireOp",EDGE,"E6.left");var subQ7=makeQuery(id+"F0.imprint","INTERSECT",VERTEX,{"derivedFrom":[subQ5,subQ3]});Q70=makeQuery(id+"F0.imprint","IMPRINT",FACE,{"disambiguationData":[TD([[makeQuery(id+"F0.imprint","IMPRINT",EDGE,{"disambiguationData":[TD([[subQ7,-1.0]])],"derivedFrom":subQ5}),-1.0]])]});}
            var Q71;
            {var subQ3=sQuery(id+"F0.wireOp",EDGE,"E77.MirrorCS");var subQ5=sQuery(id+"F0.wireOp",EDGE,"E6.right");var subQ6=makeQuery(id+"F0.imprint","INTERSECT",VERTEX,{"derivedFrom":[subQ5,subQ3]});Q71=makeQuery(id+"F0.imprint","IMPRINT",FACE,{"disambiguationData":[TD([[makeQuery(id+"F0.imprint","IMPRINT",EDGE,{"disambiguationData":[TD([[subQ6,-1.0]])],"derivedFrom":subQ5}),1.0]])]});}
            var Q72;
            {var subQ0=sQuery(id+"F0.wireOp",EDGE,"E77.MirrorCS");var subQ1=sQuery(id+"F0.wireOp",EDGE,"E0.left");var subQ2=makeQuery(id+"F0.imprint","INTERSECT",VERTEX,{"derivedFrom":[subQ1,subQ0]});Q72=makeQuery(id+"F0.imprint","IMPRINT",FACE,{"disambiguationData":[TD([[makeQuery(id+"F0.imprint","IMPRINT",EDGE,{"disambiguationData":[TD([[subQ2,-1.0]])],"derivedFrom":subQ1}),1.0]])]});}
            var Q73;
            {var subQ0=sQuery(id+"F0.wireOp",EDGE,"E77.MirrorCS");var subQ1=sQuery(id+"F0.wireOp",EDGE,"E4.MirrorCS");var subQ2=makeQuery(id+"F0.imprint","INTERSECT",VERTEX,{"derivedFrom":[subQ1,subQ0]});Q73=makeQuery(id+"F0.imprint","IMPRINT",FACE,{"disambiguationData":[TD([[makeQuery(id+"F0.imprint","IMPRINT",EDGE,{"disambiguationData":[TD([[subQ2,-1.0]])],"derivedFrom":subQ1}),-1.0]])]});}
            var Q74;
            {var subQ3=sQuery(id+"F0.wireOp",EDGE,"E77.MirrorCS");var subQ5=sQuery(id+"F0.wireOp",EDGE,"E6.left");var subQ6=makeQuery(id+"F0.imprint","INTERSECT",VERTEX,{"derivedFrom":[subQ5,subQ3]});Q74=makeQuery(id+"F0.imprint","IMPRINT",FACE,{"disambiguationData":[TD([[makeQuery(id+"F0.imprint","IMPRINT",EDGE,{"disambiguationData":[TD([[subQ6,-1.0]])],"derivedFrom":subQ5}),-1.0]])]});}
            var Q75;
            {var subQ5=sQuery(id+"F0.wireOp",EDGE,"E81.MirrorCS");Q75=makeQuery(id+"F0.imprint","IMPRINT",FACE,{"disambiguationData":[TD([[makeQuery(id+"F0.imprint","IMPRINT",EDGE,{"derivedFrom":subQ5}),1.0]])]});}
            var Q76;
            {var subQ0=sQuery(id+"F0.wireOp",EDGE,"E80.MirrorCS");var subQ1=sQuery(id+"F0.wireOp",EDGE,"E0.left");var subQ2=makeQuery(id+"F0.imprint","INTERSECT",VERTEX,{"derivedFrom":[subQ1,subQ0]});Q76=makeQuery(id+"F0.imprint","IMPRINT",FACE,{"disambiguationData":[TD([[makeQuery(id+"F0.imprint","IMPRINT",EDGE,{"disambiguationData":[TD([[subQ2,-1.0]])],"derivedFrom":subQ1}),1.0]])]});}
            var Q77;
            {var subQ0=sQuery(id+"F0.wireOp",EDGE,"E80.MirrorCS");var subQ1=sQuery(id+"F0.wireOp",EDGE,"E0.left");var subQ2=makeQuery(id+"F0.imprint","INTERSECT",VERTEX,{"derivedFrom":[subQ1,subQ0]});Q77=makeQuery(id+"F0.imprint","IMPRINT",FACE,{"disambiguationData":[TD([[makeQuery(id+"F0.imprint","IMPRINT",EDGE,{"disambiguationData":[TD([[subQ2,-1.0]])],"derivedFrom":subQ1}),-1.0]])]});}
            var Q78;
            {var subQ0=sQuery(id+"F0.wireOp",EDGE,"E80.MirrorCS");var subQ1=sQuery(id+"F0.wireOp",EDGE,"E4.MirrorCS");var subQ2=makeQuery(id+"F0.imprint","INTERSECT",VERTEX,{"derivedFrom":[subQ1,subQ0]});Q78=makeQuery(id+"F0.imprint","IMPRINT",FACE,{"disambiguationData":[TD([[makeQuery(id+"F0.imprint","IMPRINT",EDGE,{"disambiguationData":[TD([[subQ2,-1.0]])],"derivedFrom":subQ1}),-1.0]])]});}
            var Q79;
            {var subQ5=sQuery(id+"F0.wireOp",EDGE,"E75.MirrorCS");Q79=makeQuery(id+"F0.imprint","IMPRINT",FACE,{"disambiguationData":[TD([[makeQuery(id+"F0.imprint","IMPRINT",EDGE,{"derivedFrom":subQ5}),-1.0]])]});}
            var Q80;
            {var subQ5=sQuery(id+"F0.wireOp",EDGE,"E0.bottom");Q80=makeQuery(id+"F0.imprint","IMPRINT",FACE,{"disambiguationData":[TD([[makeQuery(id+"F0.imprint","IMPRINT",EDGE,{"derivedFrom":subQ5}),-1.0]])]});}
            var Q81;
            {var subQ0=sQuery(id+"F0.wireOp",EDGE,"E6.bottom");var subQ1=sQuery(id+"F0.wireOp",EDGE,"E0.left");var subQ2=makeQuery(id+"F0.imprint","INTERSECT",VERTEX,{"derivedFrom":[subQ1,subQ0]});Q81=makeQuery(id+"F0.imprint","IMPRINT",FACE,{"disambiguationData":[TD([[makeQuery(id+"F0.imprint","IMPRINT",EDGE,{"disambiguationData":[TD([[subQ2,-1.0]])],"derivedFrom":subQ1}),1.0]])]});}
            var Q82;
            {var subQ0=sQuery(id+"F0.wireOp",EDGE,"E6.bottom");var subQ1=sQuery(id+"F0.wireOp",EDGE,"E4.MirrorCS");var subQ2=makeQuery(id+"F0.imprint","INTERSECT",VERTEX,{"derivedFrom":[subQ1,subQ0]});Q82=makeQuery(id+"F0.imprint","IMPRINT",FACE,{"disambiguationData":[TD([[makeQuery(id+"F0.imprint","IMPRINT",EDGE,{"disambiguationData":[TD([[subQ2,-1.0]])],"derivedFrom":subQ1}),-1.0]])]});}
            var Q83;
            {var subQ5=sQuery(id+"F0.wireOp",EDGE,"E1.MirrorCS");Q83=makeQuery(id+"F0.imprint","IMPRINT",FACE,{"disambiguationData":[TD([[makeQuery(id+"F0.imprint","IMPRINT",EDGE,{"derivedFrom":subQ5}),1.0]])]});}
            var Q84;
            {var subQ0=sQuery(id+"F0.wireOp",EDGE,"E6.top");var subQ1=sQuery(id+"F0.wireOp",EDGE,"E0.left");var subQ2=makeQuery(id+"F0.imprint","INTERSECT",VERTEX,{"derivedFrom":[subQ1,subQ0]});Q84=makeQuery(id+"F0.imprint","IMPRINT",FACE,{"disambiguationData":[TD([[makeQuery(id+"F0.imprint","IMPRINT",EDGE,{"disambiguationData":[TD([[subQ2,1.0]])],"derivedFrom":subQ1}),1.0]])]});}
            extrude(context, id + "F1", {"entities" : qUnion([Q0, Q1, Q2, Q3, Q4, Q5, Q6, Q7, Q8, Q9, Q10, Q11, Q12, Q13, Q14, Q15, Q16, Q17, Q18, Q19, Q20, Q21, Q22, Q23, Q24, Q25, Q26, Q27, Q28, Q29, Q30, Q31, Q32, Q33, Q34, Q35, Q36, Q37, Q38, Q39, Q40, Q41, Q42, Q43, Q44, Q45, Q46, Q47, Q48, Q49, Q50, Q51, Q52, Q53, Q54, Q55, Q56, Q57, Q58, Q59, Q60, Q61, Q62, Q63, Q64, Q65, Q66, Q67, Q68, Q69, Q70, Q71, Q72, Q73, Q74, Q75, Q76, Q77, Q78, Q79, Q80, Q81, Q82, Q83, Q84]), "depth" : 27.2 * mm, "offsetDistance" : 25 * mm});
        }
        {
            var Q0;
            Q0=makeQuery(id+"F1.opExtrude","SWEPT_FACE",FACE,{"disambiguationData":[OSD([sQuery(id+"F0.wireOp",EDGE,"E80.MirrorCS")])]});
            var sketch = newSketch(context, id + "F2", { "sketchPlane" : qUnion([Q0])});
            skLineSegment(sketch, "E83", {"start": v(0, 27.2) * mm, "end": v(0, 0) * mm});
            skLineSegment(sketch, "E84.bottom", {"start": v(39.93, 2.45) * mm, "end": v(-39.93, 2.45) * mm});
            skLineSegment(sketch, "E84.top", {"start": v(39.93, 24.75) * mm, "end": v(-39.93, 24.75) * mm});
            skLineSegment(sketch, "E84.left", {"start": v(39.93, 2.45) * mm, "end": v(39.93, 24.75) * mm});
            skLineSegment(sketch, "E84.right", {"start": v(-39.93, 2.45) * mm, "end": v(-39.93, 24.75) * mm});
            skPoint(sketch, "E84.middle", {"position": v(0, 13.6) * mm});
            skSolve(sketch);
        }
        {
            var Q0;
            Q0 = qSketchRegion(id + "F2", true);
            extrude(context, id + "F3", {"entities" : qUnion([Q0]), "operationType" : NewBodyOperationType.REMOVE, "oppositeDirection" : true, "depth" : 155 * mm, "offsetDistance" : 25 * mm});
        }
    });
